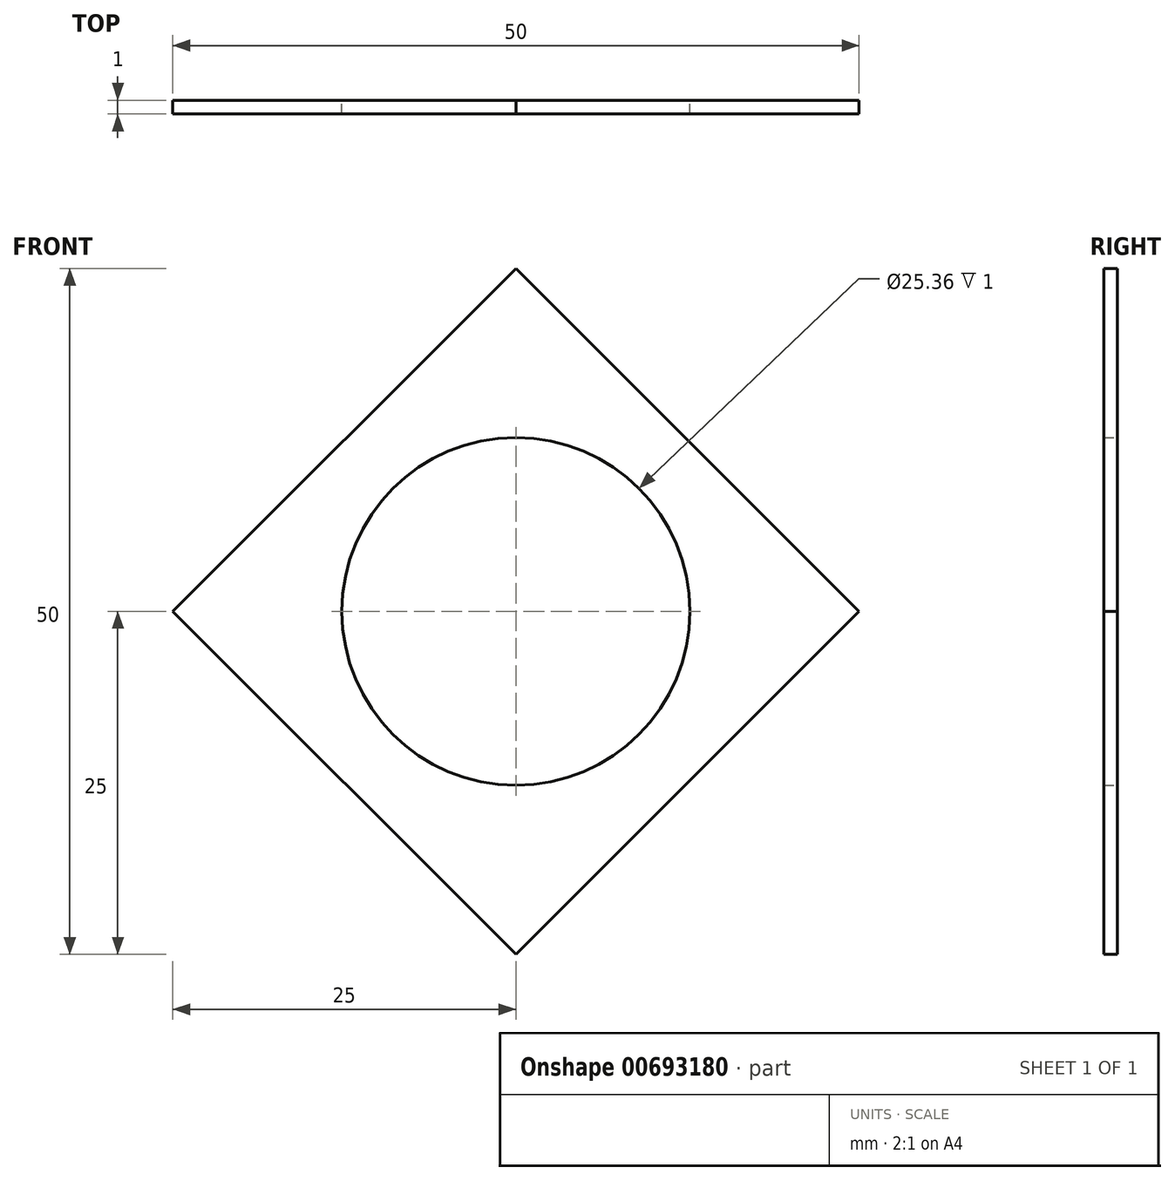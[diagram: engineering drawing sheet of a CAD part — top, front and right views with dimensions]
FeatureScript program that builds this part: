
annotation { "Feature Type Name" : "Feature", "Feature Type Description" : "" }
export const myFeature = defineFeature(function(context is Context, id is Id, definition is map)
    precondition{}
    {
        {
            var Q0;
            Q0=qCreatedBy(makeId("Front.planeOp"),FACE);
            var sketch = newSketch(context, id + "F0", { "sketchPlane" : qUnion([Q0])});
            skLineSegment(sketch, "E0", {"start": v(0, 0) * mm, "end": v(0, 25) * mm, "construction": true});
            skLineSegment(sketch, "E1", {"start": v(0, 0) * mm, "end": v(25, 0) * mm, "construction": true});
            skLineSegment(sketch, "E2", {"start": v(0, 0) * mm, "end": v(0, -25) * mm, "construction": true});
            skLineSegment(sketch, "E3", {"start": v(0, 0) * mm, "end": v(-25, 0) * mm, "construction": true});
            skLineSegment(sketch, "E4", {"start": v(-25, 0) * mm, "end": v(0, 25) * mm});
            skLineSegment(sketch, "E5", {"start": v(0, 25) * mm, "end": v(25, 0) * mm});
            skLineSegment(sketch, "E6", {"start": v(25, 0) * mm, "end": v(0, -25) * mm});
            skLineSegment(sketch, "E7", {"start": v(0, -25) * mm, "end": v(-25, 0) * mm});
            skCircle(sketch, "E8", {"center": v(0, 0) * mm, "radius": 12.68 * mm});
            skSolve(sketch);
        }
        {
            var Q0;
            Q0 = qSketchRegion(id + "F0", true);
            extrude(context, id + "F1", {"entities" : qUnion([Q0]), "depth" : 1 * mm, "offsetDistance" : 25 * mm});
        }
        {
            var Q0;
            Q0=qCreatedBy(makeId("Front.planeOp"),FACE);
            cPlane(context, id + "F2", {"entities" : qUnion([Q0]), "cplaneType" : CPlaneType.OFFSET, "offset" : 35 * mm, "width" : 150 * mm, "height" : 150 * mm});
        }
    });
